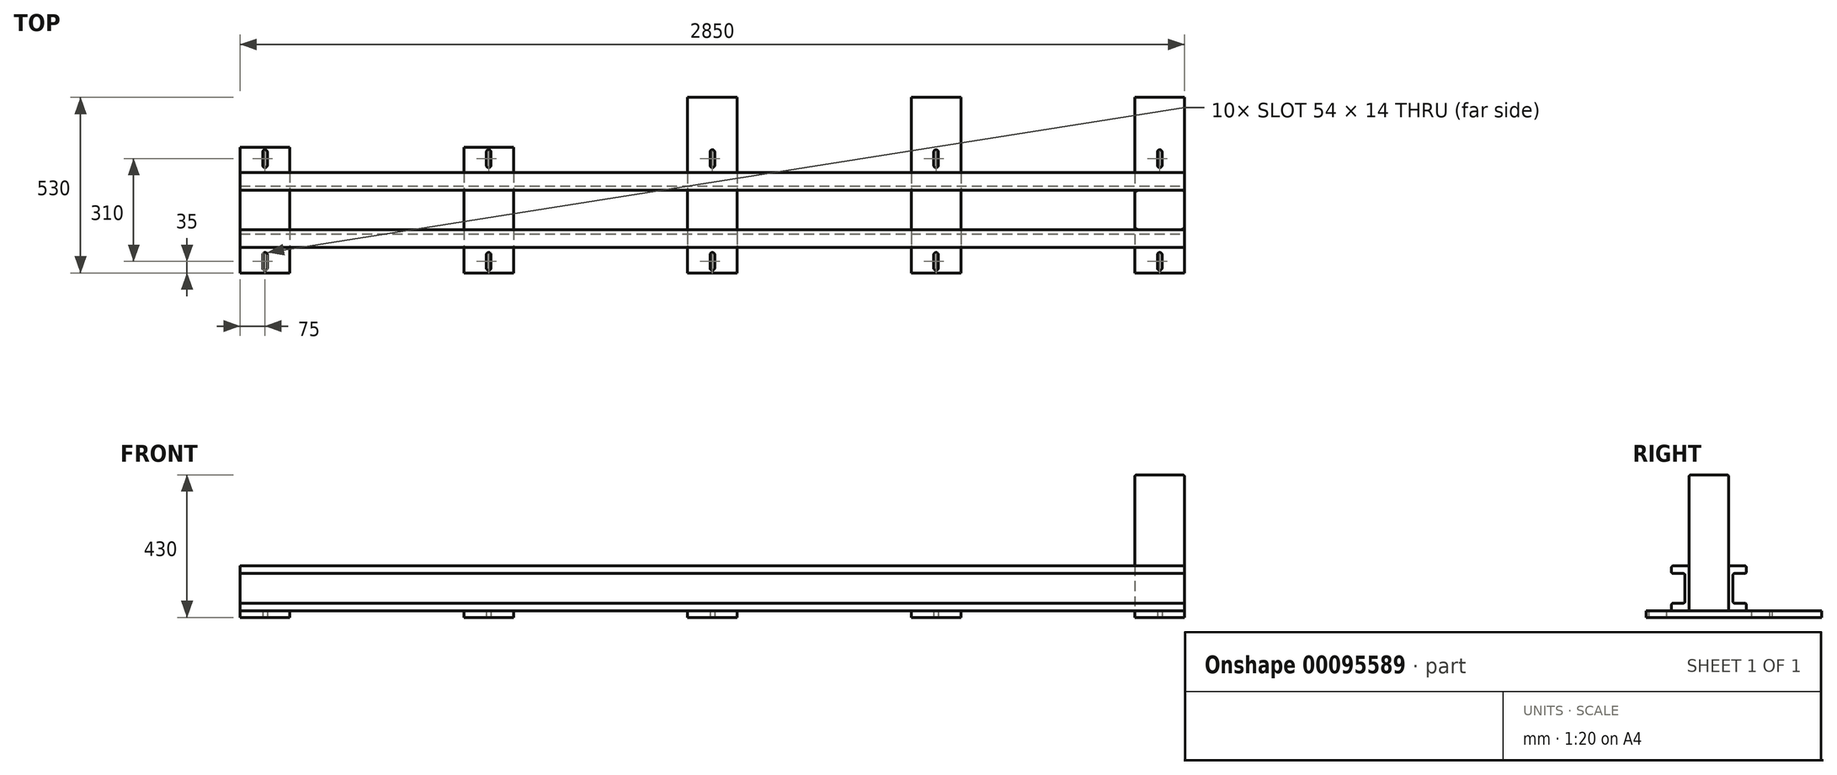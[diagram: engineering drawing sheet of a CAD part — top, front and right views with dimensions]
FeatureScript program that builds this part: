
annotation { "Feature Type Name" : "Feature", "Feature Type Description" : "" }
export const myFeature = defineFeature(function(context is Context, id is Id, definition is map)
    precondition{}
    {
        {
            var Q0;
            Q0=qCreatedBy(makeId("Top.planeOp"),FACE);
            var sketch = newSketch(context, id + "F0", { "sketchPlane" : qUnion([Q0])});
            skLineSegment(sketch, "E0", {"start": v(-1425, 0) * mm, "end": v(1425, 0) * mm, "construction": true});
            skLineSegment(sketch, "E1", {"start": v(-1425, 190) * mm, "end": v(-1425, -190) * mm, "construction": true});
            skLineSegment(sketch, "E2.bottom", {"start": v(-1425, 190) * mm, "end": v(-1275, 190) * mm});
            skLineSegment(sketch, "E2.top", {"start": v(-1425, -190) * mm, "end": v(-1275, -190) * mm});
            skLineSegment(sketch, "E2.left", {"start": v(-1425, 190) * mm, "end": v(-1425, -190) * mm});
            skLineSegment(sketch, "E2.right", {"start": v(-1275, 190) * mm, "end": v(-1275, -190) * mm});
            skLineSegment(sketch, "E3", {"start": v(-1350, 190) * mm, "end": v(-1350, -190) * mm, "construction": true});
            skLineSegment(sketch, "E4.0", {"start": v(-1425, 155) * mm, "end": v(1425, 155) * mm, "construction": true});
            skLineSegment(sketch, "E5", {"start": v(-1350, 175) * mm, "end": v(-1350, 135) * mm});
            skArc(sketch, "E6.0.startCap", {"start": v(-1357, 175) * mm, "mid": v(-1350, 182) * mm, "end": v(-1343, 175) * mm});
            skArc(sketch, "E6.0.endCap", {"start": v(-1343, 135) * mm, "mid": v(-1350, 128) * mm, "end": v(-1357, 135) * mm});
            skLineSegment(sketch, "E6.0.left", {"start": v(-1343, 175) * mm, "end": v(-1343, 135) * mm});
            skLineSegment(sketch, "E6.0.right", {"start": v(-1357, 175) * mm, "end": v(-1357, 135) * mm});
            skArc(sketch, "E7.MirrorCS", {"start": v(-1343, -135) * mm, "mid": v(-1350, -128) * mm, "end": v(-1357, -135) * mm});
            skLineSegment(sketch, "E8.MirrorCS", {"start": v(-1343, -175) * mm, "end": v(-1343, -135) * mm});
            skArc(sketch, "E9.MirrorCS", {"start": v(-1357, -175) * mm, "mid": v(-1350, -182) * mm, "end": v(-1343, -175) * mm});
            skLineSegment(sketch, "E10.MirrorCS", {"start": v(-1350, -175) * mm, "end": v(-1350, -135) * mm});
            skLineSegment(sketch, "E11.MirrorCS", {"start": v(-1357, -175) * mm, "end": v(-1357, -135) * mm});
            skLineSegment(sketch, "E12.1.0.0", {"start": v(-675, 190) * mm, "end": v(-675, -190) * mm, "construction": true});
            skLineSegment(sketch, "E12.1.0.1", {"start": v(-750, 190) * mm, "end": v(-600, 190) * mm});
            skLineSegment(sketch, "E12.1.0.2", {"start": v(-750, -190) * mm, "end": v(-600, -190) * mm});
            skLineSegment(sketch, "E12.1.0.3", {"start": v(-750, 190) * mm, "end": v(-750, -190) * mm});
            skLineSegment(sketch, "E12.1.0.4", {"start": v(-668, -175) * mm, "end": v(-668, -135) * mm});
            skLineSegment(sketch, "E12.1.0.5", {"start": v(-682, -175) * mm, "end": v(-682, -135) * mm});
            skLineSegment(sketch, "E12.1.0.6", {"start": v(-600, 190) * mm, "end": v(-600, -190) * mm});
            skLineSegment(sketch, "E12.1.0.7", {"start": v(-675, -175) * mm, "end": v(-675, -135) * mm});
            skLineSegment(sketch, "E12.1.0.8", {"start": v(-750, 190) * mm, "end": v(-750, -190) * mm, "construction": true});
            skLineSegment(sketch, "E12.1.0.9", {"start": v(-675, 175) * mm, "end": v(-675, 135) * mm});
            skLineSegment(sketch, "E12.1.0.10", {"start": v(-668, 175) * mm, "end": v(-668, 135) * mm});
            skLineSegment(sketch, "E12.1.0.11", {"start": v(-682, 175) * mm, "end": v(-682, 135) * mm});
            skArc(sketch, "E12.1.0.12", {"start": v(-682, -175) * mm, "mid": v(-675, -182) * mm, "end": v(-668, -175) * mm});
            skArc(sketch, "E12.1.0.13", {"start": v(-682, 175) * mm, "mid": v(-675, 182) * mm, "end": v(-668, 175) * mm});
            skArc(sketch, "E12.1.0.14", {"start": v(-668, -135) * mm, "mid": v(-675, -128) * mm, "end": v(-682, -135) * mm});
            skArc(sketch, "E12.1.0.15", {"start": v(-668, 135) * mm, "mid": v(-675, 128) * mm, "end": v(-682, 135) * mm});
            skLineSegment(sketch, "E12.direction1", {"start": v(-1350, -190) * mm, "end": v(-675, -190) * mm, "construction": true});
            skLineSegment(sketch, "E13", {"start": v(-675, 190) * mm, "end": v(-675, 454.32) * mm, "construction": true});
            skLineSegment(sketch, "E14.0", {"start": v(0, 190) * mm, "end": v(0, 454.32) * mm, "construction": true});
            skLineSegment(sketch, "E15.1.0.1", {"start": v(-75, -190) * mm, "end": v(75, -190) * mm});
            skLineSegment(sketch, "E15.1.0.2", {"start": v(75, 340) * mm, "end": v(75, -190) * mm});
            skLineSegment(sketch, "E15.1.0.3", {"start": v(-75, 340) * mm, "end": v(-75, -190) * mm});
            skLineSegment(sketch, "E15.1.0.4", {"start": v(0, 190) * mm, "end": v(0, -190) * mm, "construction": true});
            skLineSegment(sketch, "E15.1.0.5", {"start": v(-75, 190) * mm, "end": v(-75, -190) * mm, "construction": true});
            skLineSegment(sketch, "E15.1.0.6", {"start": v(0, 175) * mm, "end": v(0, 135) * mm});
            skLineSegment(sketch, "E15.1.0.7", {"start": v(-7, -175) * mm, "end": v(-7, -135) * mm});
            skLineSegment(sketch, "E15.1.0.8", {"start": v(-7, 175) * mm, "end": v(-7, 135) * mm});
            skLineSegment(sketch, "E15.1.0.9", {"start": v(7, 175) * mm, "end": v(7, 135) * mm});
            skArc(sketch, "E15.1.0.10", {"start": v(-7, -175) * mm, "mid": v(0, -182) * mm, "end": v(7, -175) * mm});
            skArc(sketch, "E15.1.0.11", {"start": v(7, 135) * mm, "mid": v(0, 128) * mm, "end": v(-7, 135) * mm});
            skLineSegment(sketch, "E15.1.0.12", {"start": v(0, -175) * mm, "end": v(0, -135) * mm});
            skLineSegment(sketch, "E15.1.0.13", {"start": v(7, -175) * mm, "end": v(7, -135) * mm});
            skArc(sketch, "E15.1.0.14", {"start": v(-7, 175) * mm, "mid": v(0, 182) * mm, "end": v(7, 175) * mm});
            skArc(sketch, "E15.1.0.15", {"start": v(7, -135) * mm, "mid": v(0, -128) * mm, "end": v(-7, -135) * mm});
            skLineSegment(sketch, "E15.direction1", {"start": v(-750, 190) * mm, "end": v(-75, 190) * mm, "construction": true});
            skLineSegment(sketch, "E16.0", {"start": v(-75, 340) * mm, "end": v(75, 340) * mm});
            skPoint(sketch, "E17.orphan", {"position": v(75, 190) * mm});
            skLineSegment(sketch, "E18.1.0.0", {"start": v(600, 340) * mm, "end": v(750, 340) * mm});
            skLineSegment(sketch, "E18.1.0.1", {"start": v(675, 190) * mm, "end": v(675, -190) * mm, "construction": true});
            skLineSegment(sketch, "E18.1.0.2", {"start": v(600, -190) * mm, "end": v(750, -190) * mm});
            skLineSegment(sketch, "E18.1.0.3", {"start": v(600, 340) * mm, "end": v(600, -190) * mm});
            skPoint(sketch, "E18.1.0.4", {"position": v(750, 190) * mm});
            skLineSegment(sketch, "E18.1.0.5", {"start": v(750, 340) * mm, "end": v(750, -190) * mm});
            skLineSegment(sketch, "E18.1.0.6", {"start": v(600, 190) * mm, "end": v(600, -190) * mm, "construction": true});
            skLineSegment(sketch, "E18.1.0.7", {"start": v(675, -175) * mm, "end": v(675, -135) * mm});
            skLineSegment(sketch, "E18.1.0.8", {"start": v(682, 175) * mm, "end": v(682, 135) * mm});
            skArc(sketch, "E18.1.0.9", {"start": v(668, -175) * mm, "mid": v(675, -182) * mm, "end": v(682, -175) * mm});
            skLineSegment(sketch, "E18.1.0.10", {"start": v(668, 175) * mm, "end": v(668, 135) * mm});
            skLineSegment(sketch, "E18.1.0.11", {"start": v(668, -175) * mm, "end": v(668, -135) * mm});
            skLineSegment(sketch, "E18.1.0.12", {"start": v(682, -175) * mm, "end": v(682, -135) * mm});
            skArc(sketch, "E18.1.0.13", {"start": v(682, -135) * mm, "mid": v(675, -128) * mm, "end": v(668, -135) * mm});
            skArc(sketch, "E18.1.0.14", {"start": v(682, 135) * mm, "mid": v(675, 128) * mm, "end": v(668, 135) * mm});
            skArc(sketch, "E18.1.0.15", {"start": v(668, 175) * mm, "mid": v(675, 182) * mm, "end": v(682, 175) * mm});
            skLineSegment(sketch, "E18.1.0.16", {"start": v(675, 175) * mm, "end": v(675, 135) * mm});
            skLineSegment(sketch, "E18.2.0.0", {"start": v(1275, 340) * mm, "end": v(1425, 340) * mm});
            skLineSegment(sketch, "E18.2.0.1", {"start": v(1350, 190) * mm, "end": v(1350, -190) * mm, "construction": true});
            skLineSegment(sketch, "E18.2.0.2", {"start": v(1275, -190) * mm, "end": v(1425, -190) * mm});
            skLineSegment(sketch, "E18.2.0.3", {"start": v(1275, 340) * mm, "end": v(1275, -190) * mm});
            skPoint(sketch, "E18.2.0.4", {"position": v(1425, 190) * mm});
            skLineSegment(sketch, "E18.2.0.5", {"start": v(1425, 340) * mm, "end": v(1425, -190) * mm});
            skLineSegment(sketch, "E18.2.0.6", {"start": v(1275, 190) * mm, "end": v(1275, -190) * mm, "construction": true});
            skLineSegment(sketch, "E18.2.0.7", {"start": v(1350, -175) * mm, "end": v(1350, -135) * mm});
            skLineSegment(sketch, "E18.2.0.8", {"start": v(1357, 175) * mm, "end": v(1357, 135) * mm});
            skArc(sketch, "E18.2.0.9", {"start": v(1343, -175) * mm, "mid": v(1350, -182) * mm, "end": v(1357, -175) * mm});
            skLineSegment(sketch, "E18.2.0.10", {"start": v(1343, 175) * mm, "end": v(1343, 135) * mm});
            skLineSegment(sketch, "E18.2.0.11", {"start": v(1343, -175) * mm, "end": v(1343, -135) * mm});
            skLineSegment(sketch, "E18.2.0.12", {"start": v(1357, -175) * mm, "end": v(1357, -135) * mm});
            skArc(sketch, "E18.2.0.13", {"start": v(1357, -135) * mm, "mid": v(1350, -128) * mm, "end": v(1343, -135) * mm});
            skArc(sketch, "E18.2.0.14", {"start": v(1357, 135) * mm, "mid": v(1350, 128) * mm, "end": v(1343, 135) * mm});
            skArc(sketch, "E18.2.0.15", {"start": v(1343, 175) * mm, "mid": v(1350, 182) * mm, "end": v(1357, 175) * mm});
            skLineSegment(sketch, "E18.2.0.16", {"start": v(1350, 175) * mm, "end": v(1350, 135) * mm});
            skLineSegment(sketch, "E18.direction1", {"start": v(-75, 340) * mm, "end": v(600, 340) * mm, "construction": true});
            skSolve(sketch);
        }
        {
            var Q0;
            Q0 = qSketchRegion(id + "F0", true);
            extrude(context, id + "F1", {"entities" : qUnion([Q0]), "depth" : 20 * mm});
        }
        {
            var Q0;
            Q0=makeQuery(id+"F1.opExtrude","SWEPT_FACE",FACE,{"disambiguationData":[OSD([sQuery(id+"F0.wireOp",EDGE,"E18.2.0.5")])]});
            var sketch = newSketch(context, id + "F2", { "sketchPlane" : qUnion([Q0])});
            skLineSegment(sketch, "E19", {"start": v(0, -122.87) * mm, "end": v(0, 210.37) * mm, "construction": true});
            skLineSegment(sketch, "E20.0", {"start": v(340, 20) * mm, "end": v(-190, 20) * mm, "construction": true});
            skLineSegment(sketch, "E21.0", {"start": v(340, 155.5) * mm, "end": v(-190, 155.5) * mm, "construction": true});
            skLineSegment(sketch, "E22.0", {"start": v(-60, -122.87) * mm, "end": v(-60, 210.37) * mm, "construction": true});
            skLineSegment(sketch, "E23.0", {"start": v(-113, -122.87) * mm, "end": v(-113, 210.37) * mm, "construction": true});
            skLineSegment(sketch, "E24.0", {"start": v(-72.5, -122.87) * mm, "end": v(-72.5, 210.37) * mm, "construction": true});
            skLineSegment(sketch, "E25.0", {"start": v(340, 43) * mm, "end": v(-190, 43) * mm, "construction": true});
            skLineSegment(sketch, "E26.0", {"start": v(340, 132.5) * mm, "end": v(-190, 132.5) * mm, "construction": true});
            skLineSegment(sketch, "E27", {"start": v(-65, 155.5) * mm, "end": v(-108, 155.5) * mm});
            skLineSegment(sketch, "E28", {"start": v(-113, 150.5) * mm, "end": v(-113, 137.5) * mm});
            skLineSegment(sketch, "E29", {"start": v(-108, 132.5) * mm, "end": v(-77.5, 132.5) * mm});
            skLineSegment(sketch, "E30", {"start": v(-72.5, 127.5) * mm, "end": v(-72.5, 48) * mm});
            skLineSegment(sketch, "E31", {"start": v(-77.5, 43) * mm, "end": v(-108, 43) * mm});
            skLineSegment(sketch, "E32", {"start": v(-113, 38) * mm, "end": v(-113, 25) * mm});
            skLineSegment(sketch, "E33", {"start": v(-108, 20) * mm, "end": v(-65, 20) * mm});
            skLineSegment(sketch, "E34", {"start": v(-60, 25) * mm, "end": v(-60, 150.5) * mm});
            skPoint(sketch, "E35.visualSharp", {"position": v(-113, 155.5) * mm});
            skArc(sketch, "E35.filletArc", {"start": v(-108, 155.5) * mm, "mid": v(-111.54, 154.04) * mm, "end": v(-113, 150.5) * mm});
            skPoint(sketch, "E36.visualSharp", {"position": v(-113, 132.5) * mm});
            skArc(sketch, "E36.filletArc", {"start": v(-113, 137.5) * mm, "mid": v(-111.54, 133.96) * mm, "end": v(-108, 132.5) * mm});
            skPoint(sketch, "E37.visualSharp", {"position": v(-72.5, 132.5) * mm});
            skArc(sketch, "E37.filletArc", {"start": v(-72.5, 127.5) * mm, "mid": v(-73.96, 131.04) * mm, "end": v(-77.5, 132.5) * mm});
            skPoint(sketch, "E38.visualSharp", {"position": v(-72.5, 43) * mm});
            skArc(sketch, "E38.filletArc", {"start": v(-77.5, 43) * mm, "mid": v(-73.96, 44.46) * mm, "end": v(-72.5, 48) * mm});
            skPoint(sketch, "E39.visualSharp", {"position": v(-113, 43) * mm});
            skArc(sketch, "E39.filletArc", {"start": v(-108, 43) * mm, "mid": v(-111.54, 41.54) * mm, "end": v(-113, 38) * mm});
            skPoint(sketch, "E40.visualSharp", {"position": v(-113, 20) * mm});
            skArc(sketch, "E40.filletArc", {"start": v(-113, 25) * mm, "mid": v(-111.54, 21.46) * mm, "end": v(-108, 20) * mm});
            skPoint(sketch, "E41.visualSharp", {"position": v(-60, 20) * mm});
            skArc(sketch, "E41.filletArc", {"start": v(-65, 20) * mm, "mid": v(-61.46, 21.46) * mm, "end": v(-60, 25) * mm});
            skPoint(sketch, "E42.visualSharp", {"position": v(-60, 155.5) * mm});
            skArc(sketch, "E42.filletArc", {"start": v(-60, 150.5) * mm, "mid": v(-61.46, 154.04) * mm, "end": v(-65, 155.5) * mm});
            skArc(sketch, "E43.MirrorCS", {"start": v(60, 150.5) * mm, "mid": v(61.46, 154.04) * mm, "end": v(65, 155.5) * mm});
            skArc(sketch, "E44.MirrorCS", {"start": v(65, 20) * mm, "mid": v(61.46, 21.46) * mm, "end": v(60, 25) * mm});
            skArc(sketch, "E45.MirrorCS", {"start": v(72.5, 127.5) * mm, "mid": v(73.96, 131.04) * mm, "end": v(77.5, 132.5) * mm});
            skArc(sketch, "E46.MirrorCS", {"start": v(108, 155.5) * mm, "mid": v(111.54, 154.04) * mm, "end": v(113, 150.5) * mm});
            skArc(sketch, "E47.MirrorCS", {"start": v(113, 25) * mm, "mid": v(111.54, 21.46) * mm, "end": v(108, 20) * mm});
            skLineSegment(sketch, "E48.MirrorCS", {"start": v(113, 150.5) * mm, "end": v(113, 137.5) * mm});
            skLineSegment(sketch, "E49.MirrorCS", {"start": v(113, 38) * mm, "end": v(113, 25) * mm});
            skArc(sketch, "E50.MirrorCS", {"start": v(108, 43) * mm, "mid": v(111.54, 41.54) * mm, "end": v(113, 38) * mm});
            skArc(sketch, "E51.MirrorCS", {"start": v(113, 137.5) * mm, "mid": v(111.54, 133.96) * mm, "end": v(108, 132.5) * mm});
            skArc(sketch, "E52.MirrorCS", {"start": v(77.5, 43) * mm, "mid": v(73.96, 44.46) * mm, "end": v(72.5, 48) * mm});
            skLineSegment(sketch, "E53.MirrorCS", {"start": v(65, 155.5) * mm, "end": v(108, 155.5) * mm});
            skLineSegment(sketch, "E54.MirrorCS", {"start": v(108, 132.5) * mm, "end": v(77.5, 132.5) * mm});
            skLineSegment(sketch, "E55.MirrorCS", {"start": v(60, 25) * mm, "end": v(60, 150.5) * mm});
            skLineSegment(sketch, "E56.MirrorCS", {"start": v(72.5, 127.5) * mm, "end": v(72.5, 48) * mm});
            skLineSegment(sketch, "E57.MirrorCS", {"start": v(77.5, 43) * mm, "end": v(108, 43) * mm});
            skPoint(sketch, "E58.MirrorP", {"position": v(113, 132.5) * mm});
            skLineSegment(sketch, "E59.MirrorCS", {"start": v(108, 20) * mm, "end": v(65, 20) * mm});
            skPoint(sketch, "E60.MirrorP", {"position": v(72.5, 132.5) * mm});
            skPoint(sketch, "E61.MirrorP", {"position": v(113, 155.5) * mm});
            skPoint(sketch, "E62.MirrorP", {"position": v(72.5, 43) * mm});
            skPoint(sketch, "E63.MirrorP", {"position": v(113, 43) * mm});
            skPoint(sketch, "E64.MirrorP", {"position": v(113, 20) * mm});
            skPoint(sketch, "E65.MirrorP", {"position": v(60, 20) * mm});
            skPoint(sketch, "E66.MirrorP", {"position": v(60, 155.5) * mm});
            skSolve(sketch);
        }
        {
            var Q0;
            Q0 = qSketchRegion(id + "F2", true);
            extrude(context, id + "F3", {"entities" : qUnion([Q0]), "oppositeDirection" : true, "depth" : 2850 * mm});
        }
        {
            var Q0;
            Q0=makeQuery(id+"F1.opExtrude","CAP_FACE",FACE,{"disambiguationData":[OSD([sQuery(id+"F0.wireOp",EDGE,"E18.2.0.0"),sQuery(id+"F0.wireOp",EDGE,"E18.2.0.2"),sQuery(id+"F0.wireOp",EDGE,"E18.2.0.3"),sQuery(id+"F0.wireOp",EDGE,"E18.2.0.5"),sQuery(id+"F0.wireOp",EDGE,"E18.2.0.8"),sQuery(id+"F0.wireOp",EDGE,"E18.2.0.9"),sQuery(id+"F0.wireOp",EDGE,"E18.2.0.10"),sQuery(id+"F0.wireOp",EDGE,"E18.2.0.11"),sQuery(id+"F0.wireOp",EDGE,"E18.2.0.12"),sQuery(id+"F0.wireOp",EDGE,"E18.2.0.13"),sQuery(id+"F0.wireOp",EDGE,"E18.2.0.14"),sQuery(id+"F0.wireOp",EDGE,"E18.2.0.15")])],"isStart":false});
            var sketch = newSketch(context, id + "F4", { "sketchPlane" : qUnion([Q0])});
            skLineSegment(sketch, "E67.0", {"start": v(1275, 340) * mm, "end": v(1275, -190) * mm, "construction": true});
            skLineSegment(sketch, "E68.0", {"start": v(1425, 340) * mm, "end": v(1425, -190) * mm, "construction": true});
            skLineSegment(sketch, "E69.0", {"start": v(-1425, 60) * mm, "end": v(1425, 60) * mm, "construction": true});
            skLineSegment(sketch, "E70.0", {"start": v(-1425, -60) * mm, "end": v(1425, -60) * mm, "construction": true});
            skLineSegment(sketch, "E71.bottom", {"start": v(1425, 60) * mm, "end": v(1275, 60) * mm});
            skLineSegment(sketch, "E71.top", {"start": v(1425, -60) * mm, "end": v(1275, -60) * mm});
            skLineSegment(sketch, "E71.left", {"start": v(1425, 60) * mm, "end": v(1425, -60) * mm});
            skLineSegment(sketch, "E71.right", {"start": v(1275, 60) * mm, "end": v(1275, -60) * mm});
            skSolve(sketch);
        }
        {
            var Q0;
            Q0 = qSketchRegion(id + "F4", true);
            extrude(context, id + "F5", {"entities" : qUnion([Q0]), "depth" : 410 * mm});
        }
        {
            var Q0;
            Q0=makeQuery(id+"F5.opExtrude","CAP_FACE",FACE,{"disambiguationData":[OSD([sQuery(id+"F4.wireOp",EDGE,"E71.bottom"),sQuery(id+"F4.wireOp",EDGE,"E71.top"),sQuery(id+"F4.wireOp",EDGE,"E71.left"),sQuery(id+"F4.wireOp",EDGE,"E71.right")])],"isStart":false});
            fillet(context, id + "F6", {"entities" : qUnion([Q0]), "radius" : 5 * mm, "tangentPropagation" : true, "allowEdgeOverflow" : false});
        }
    });
